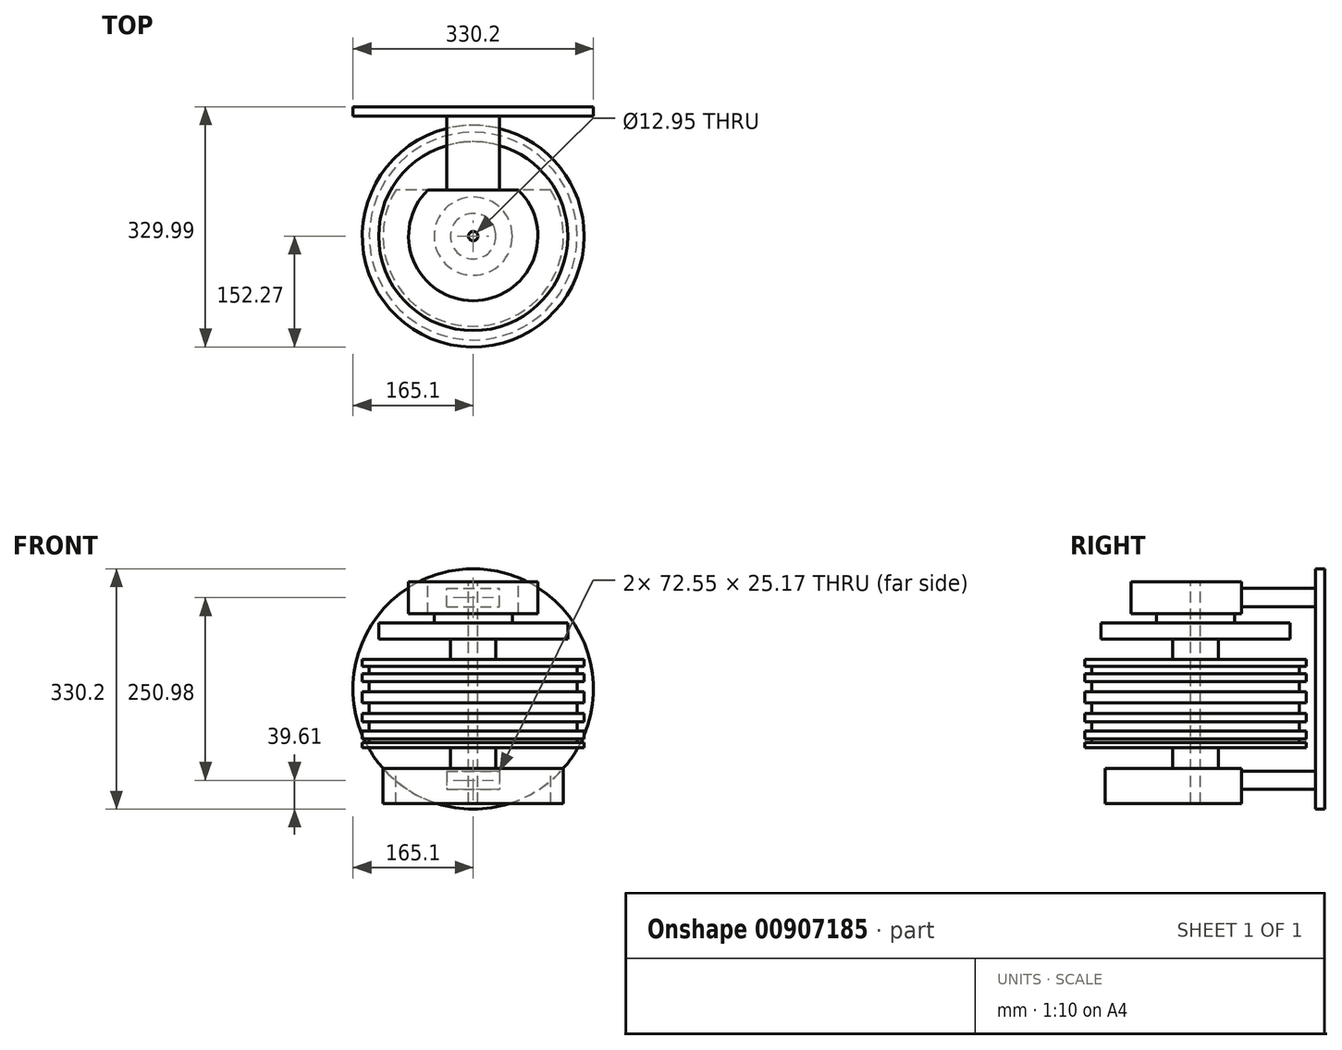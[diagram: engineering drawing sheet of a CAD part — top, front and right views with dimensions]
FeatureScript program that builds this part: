
annotation { "Feature Type Name" : "Feature", "Feature Type Description" : "" }
export const myFeature = defineFeature(function(context is Context, id is Id, definition is map)
    precondition{}
    {
        {
            var Q0;
            Q0=qCreatedBy(makeId("Front.planeOp"),FACE);
            var sketch = newSketch(context, id + "F0", { "sketchPlane" : qUnion([Q0])});
            skLineSegment(sketch, "E0", {"start": v(0, 147.41) * mm, "end": v(0, -157.39) * mm, "construction": true});
            skLineSegment(sketch, "E1", {"start": v(6.48, 147.41) * mm, "end": v(88.8, 147.41) * mm});
            skLineSegment(sketch, "E2", {"start": v(88.8, 147.41) * mm, "end": v(88.8, 103.57) * mm});
            skLineSegment(sketch, "E3", {"start": v(88.8, 103.57) * mm, "end": v(53.75, 103.57) * mm});
            skLineSegment(sketch, "E4", {"start": v(53.75, 103.57) * mm, "end": v(53.75, 91) * mm});
            skLineSegment(sketch, "E5", {"start": v(53.75, 91) * mm, "end": v(129.8, 91) * mm});
            skLineSegment(sketch, "E6", {"start": v(129.8, 91) * mm, "end": v(129.8, 68.52) * mm});
            skLineSegment(sketch, "E7", {"start": v(129.8, 68.52) * mm, "end": v(31.27, 68.52) * mm});
            skLineSegment(sketch, "E8", {"start": v(31.27, 68.52) * mm, "end": v(31.27, 40.75) * mm});
            skLineSegment(sketch, "E9", {"start": v(31.27, 40.75) * mm, "end": v(152.27, 40.75) * mm});
            skLineSegment(sketch, "E10", {"start": v(152.27, -80.91) * mm, "end": v(31.27, -80.91) * mm});
            skLineSegment(sketch, "E11", {"start": v(31.27, -80.91) * mm, "end": v(31.27, -109.35) * mm});
            skLineSegment(sketch, "E12", {"start": v(31.27, -109.35) * mm, "end": v(123.84, -109.35) * mm});
            skLineSegment(sketch, "E13", {"start": v(123.84, -109.35) * mm, "end": v(123.84, -157.39) * mm});
            skLineSegment(sketch, "E14", {"start": v(123.84, -157.39) * mm, "end": v(6.48, -157.39) * mm});
            skLineSegment(sketch, "E15", {"start": v(152.27, 40.75) * mm, "end": v(152.27, 30.77) * mm});
            skLineSegment(sketch, "E16", {"start": v(152.27, 30.77) * mm, "end": v(142.72, 30.77) * mm});
            skLineSegment(sketch, "E17", {"start": v(142.72, 30.77) * mm, "end": v(142.72, 20.72) * mm});
            skLineSegment(sketch, "E18", {"start": v(142.72, 20.72) * mm, "end": v(152.27, 20.72) * mm});
            skLineSegment(sketch, "E19", {"start": v(152.27, 20.72) * mm, "end": v(152.27, 10.2) * mm});
            skLineSegment(sketch, "E20", {"start": v(152.27, 10.2) * mm, "end": v(142.72, 10.2) * mm});
            skLineSegment(sketch, "E21", {"start": v(142.72, 10.2) * mm, "end": v(142.72, -4.06) * mm});
            skLineSegment(sketch, "E22", {"start": v(142.72, -4.06) * mm, "end": v(152.27, -4.06) * mm});
            skLineSegment(sketch, "E23", {"start": v(152.27, -4.06) * mm, "end": v(152.27, -19.02) * mm});
            skLineSegment(sketch, "E24", {"start": v(152.27, -19.02) * mm, "end": v(142.72, -19.02) * mm});
            skLineSegment(sketch, "E25", {"start": v(142.72, -19.02) * mm, "end": v(142.72, -33.52) * mm});
            skLineSegment(sketch, "E26", {"start": v(142.72, -33.52) * mm, "end": v(152.27, -33.52) * mm});
            skLineSegment(sketch, "E27", {"start": v(152.27, -33.52) * mm, "end": v(152.27, -45.44) * mm});
            skLineSegment(sketch, "E28", {"start": v(152.27, -45.44) * mm, "end": v(142.72, -45.44) * mm});
            skLineSegment(sketch, "E29", {"start": v(142.72, -45.44) * mm, "end": v(142.72, -57.6) * mm});
            skLineSegment(sketch, "E30", {"start": v(142.72, -57.6) * mm, "end": v(152.27, -57.6) * mm});
            skLineSegment(sketch, "E31", {"start": v(152.27, -57.6) * mm, "end": v(152.27, -68.59) * mm});
            skLineSegment(sketch, "E32", {"start": v(152.27, -68.59) * mm, "end": v(142.72, -68.59) * mm});
            skLineSegment(sketch, "E33", {"start": v(142.72, -68.59) * mm, "end": v(142.72, -73.55) * mm});
            skLineSegment(sketch, "E34", {"start": v(142.72, -73.55) * mm, "end": v(152.27, -73.55) * mm});
            skLineSegment(sketch, "E35", {"start": v(152.27, -73.55) * mm, "end": v(152.27, -80.91) * mm});
            skLineSegment(sketch, "E36", {"start": v(6.48, 147.41) * mm, "end": v(6.48, -157.39) * mm});
            skSolve(sketch);
        }
        {
            var Q0;
            Q0 = qSketchRegion(id + "F0", true);
            var Q1;
            Q1=sQuery(id+"F0.wireOp",EDGE,"E0");
            revolve(context, id + "F1", {"surfaceOperationType" : NewSurfaceOperationType.NEW, "entities" : qUnion([Q0]), "axis" : qUnion([Q1]), "revolveType" : RevolveType.FULL});
        }
        {
            var Q0;
            Q0=qCreatedBy(makeId("Right.planeOp"),FACE);
            var sketch = newSketch(context, id + "F2", { "sketchPlane" : qUnion([Q0])});
            skLineSegment(sketch, "E37.bottom", {"start": v(63.42, 198.8) * mm, "end": v(159.36, 198.8) * mm});
            skLineSegment(sketch, "E37.top", {"start": v(63.42, 95.79) * mm, "end": v(159.36, 95.79) * mm});
            skLineSegment(sketch, "E37.left", {"start": v(63.42, 198.8) * mm, "end": v(63.42, 95.79) * mm});
            skLineSegment(sketch, "E37.right", {"start": v(159.36, 198.8) * mm, "end": v(159.36, 95.79) * mm});
            skLineSegment(sketch, "E38", {"start": v(63.42, -96.83) * mm, "end": v(63.42, -198.3) * mm});
            skLineSegment(sketch, "E39", {"start": v(159.36, -96.83) * mm, "end": v(159.36, -196.7) * mm});
            skLineSegment(sketch, "E40", {"start": v(63.42, -96.83) * mm, "end": v(159.36, -96.83) * mm});
            skLineSegment(sketch, "E41", {"start": v(63.42, -198.3) * mm, "end": v(159.36, -196.7) * mm});
            skSolve(sketch);
        }
        {
            var Q0;
            Q0 = qSketchRegion(id + "F2", true);
            extrude(context, id + "F3", {"entities" : qUnion([Q0]), "operationType" : NewBodyOperationType.REMOVE, "endBound" : BoundingType.SYMMETRIC, "oppositeDirection" : true, "depth" : 254 * mm, "offsetDistance" : 25.4 * mm});
        }
        {
            var Q0;
            Q0=makeQuery(id+"F3.boolean.opBoolean","COPY",FACE,{"derivedFrom":makeQuery(id+"F3.opExtrude","SWEPT_FACE",FACE,{"disambiguationData":[OSD([sQuery(id+"F2.wireOp",EDGE,"E37.left")])]})});
            var sketch = newSketch(context, id + "F4", { "sketchPlane" : qUnion([Q0])});
            skLineSegment(sketch, "E42.bottom", {"start": v(36.28, 112.9) * mm, "end": v(-36.28, 112.9) * mm});
            skLineSegment(sketch, "E42.top", {"start": v(36.28, 138.07) * mm, "end": v(-36.28, 138.07) * mm});
            skLineSegment(sketch, "E42.left", {"start": v(36.28, 112.9) * mm, "end": v(36.28, 138.07) * mm});
            skLineSegment(sketch, "E42.right", {"start": v(-36.28, 112.9) * mm, "end": v(-36.28, 138.07) * mm});
            skPoint(sketch, "E42.middle", {"position": v(0, 125.5) * mm});
            skPoint(sketch, "E42.middle.positionSnap0", {"position": v(-62.15, 125.5) * mm});
            skPoint(sketch, "E42.centerSnap0", {"position": v(-62.15, 125.5) * mm});
            skLineSegment(sketch, "E43.MirrorCS", {"start": v(36.28, -112.9) * mm, "end": v(-36.28, -112.9) * mm});
            skLineSegment(sketch, "E44.MirrorCS", {"start": v(36.28, -112.9) * mm, "end": v(36.28, -138.07) * mm});
            skLineSegment(sketch, "E45.MirrorCS", {"start": v(36.28, -138.07) * mm, "end": v(-36.28, -138.07) * mm});
            skLineSegment(sketch, "E46.MirrorCS", {"start": v(-36.28, -112.9) * mm, "end": v(-36.28, -138.07) * mm});
            skSolve(sketch);
        }
        {
            var Q0;
            Q0 = qSketchRegion(id + "F4", true);
            extrude(context, id + "F5", {"entities" : qUnion([Q0]), "operationType" : NewBodyOperationType.ADD, "depth" : 101.6 * mm, "offsetDistance" : 25.4 * mm});
        }
        {
            var Q0;
            Q0=makeQuery(id+"F5.opExtrude","CAP_FACE",FACE,{"disambiguationData":[OSD([sQuery(id+"F4.wireOp",EDGE,"E42.bottom"),sQuery(id+"F4.wireOp",EDGE,"E42.top"),sQuery(id+"F4.wireOp",EDGE,"E42.left"),sQuery(id+"F4.wireOp",EDGE,"E42.right")])],"isStart":false});
            var sketch = newSketch(context, id + "F6", { "sketchPlane" : qUnion([Q0])});
            skCircle(sketch, "E47", {"center": v(0, 0) * mm, "radius": 165.1 * mm});
            skSolve(sketch);
        }
        {
            var Q0;
            Q0 = qSketchRegion(id + "F6", true);
            extrude(context, id + "F7", {"entities" : qUnion([Q0]), "operationType" : NewBodyOperationType.ADD, "depth" : 12.7 * mm, "offsetDistance" : 25.4 * mm});
        }
    });
